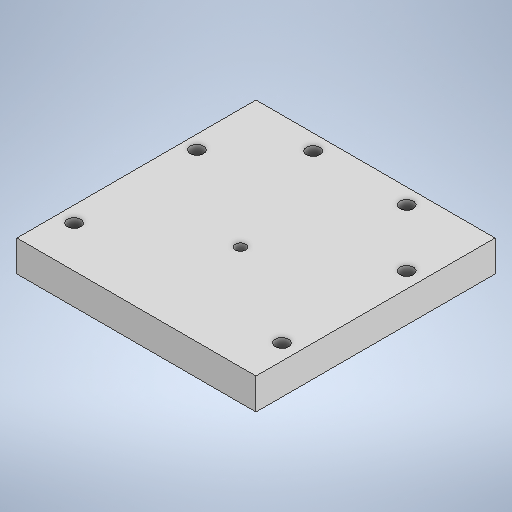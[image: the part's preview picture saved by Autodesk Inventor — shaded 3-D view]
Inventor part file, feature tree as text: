
AUTODESK INVENTOR PART (.ipt)
format: ipt  version: 2025 (Build 290162010, 162A)  size: 248,320 bytes
history: native  units: in
note: dims shown in document units (in); Inventor stores cm internally (conversion verified against a paired STEP export)
features: extrude x3, sketch x3
ambient origin geometry x8: Origin, YZ Plane, XZ Plane, XY Plane, X Axis, Y Axis, Z Axis, Center Point
bodies: Solid1 (feature_tree)
feature tree (6):
  extrude  "Extrusion1"  Depth=5.75in
  extrude  "Extrusion2"  Depth=0.75in
  extrude  "Extrusion3"  Depth=0.75in
  sketch  "Sketch1"  dims[d2=5.75in d3=5.75in]
  sketch  "Sketch2"  dims[d4=0.75in d5=0.0in d6=0.25in]
  sketch  "Sketch3"  dims[d7=3.25in d8=2.875in d9=0.75in d10=0.0in d11=0.322in d12=0.375in d13=1.0in d14=0.322in d15=4.0in d16=0.322in d17=1.0in d18=0.375in d19=0.322in d20=0.375in d21=4.0in d22=0.322in d23=1.75in d24=0.375in d25=0.322in d26=4.0in d27=0.75in d28=0.0in]
